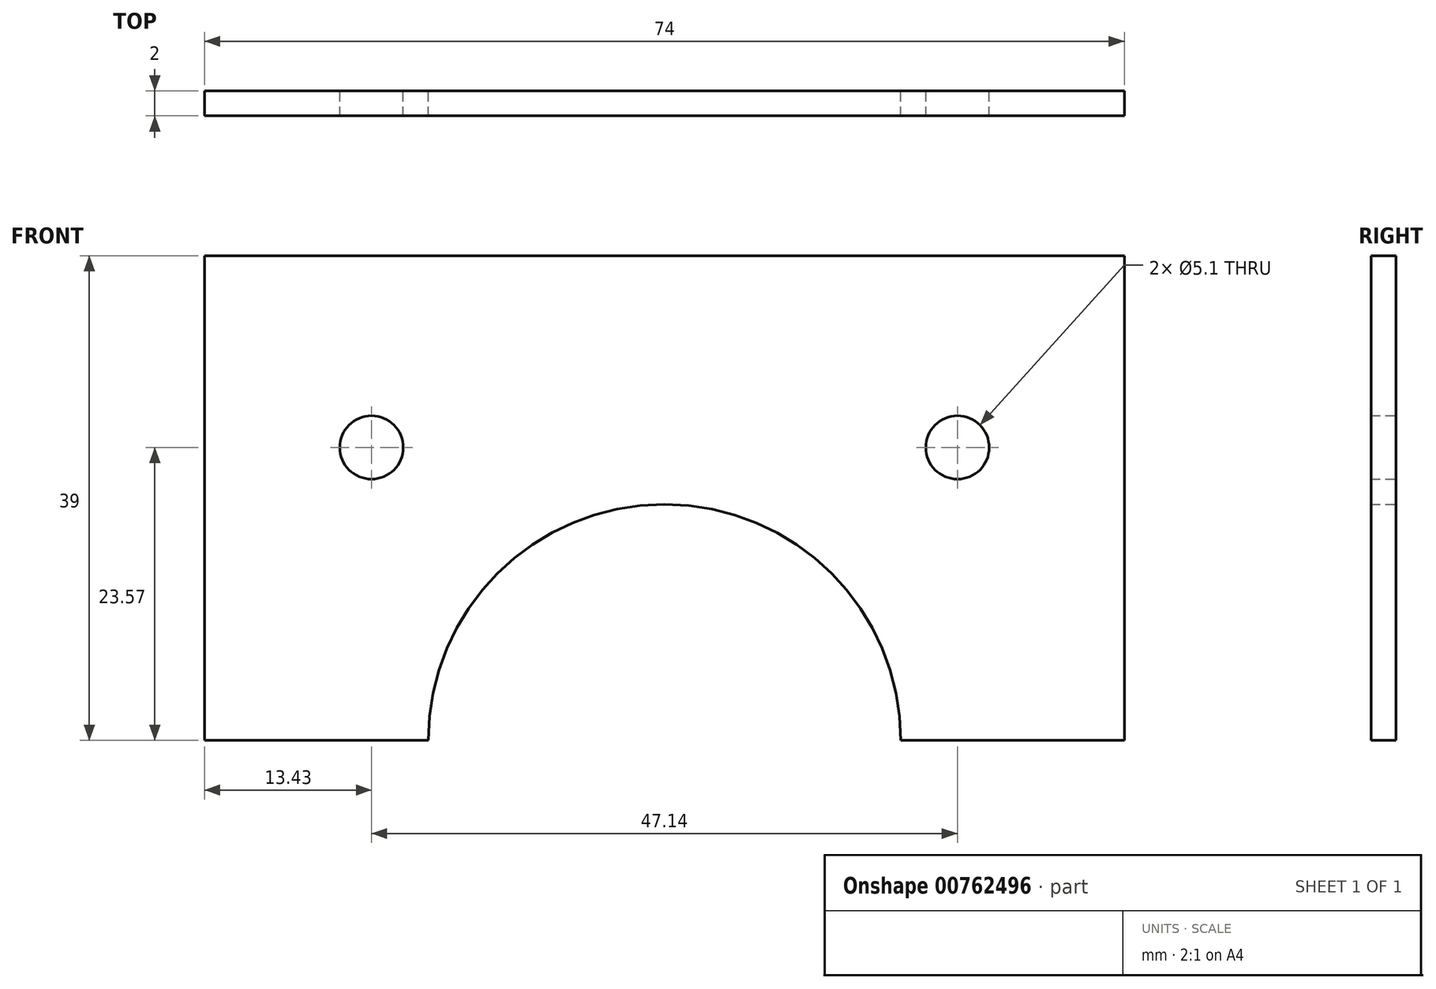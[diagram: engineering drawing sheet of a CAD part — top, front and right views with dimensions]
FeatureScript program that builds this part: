
annotation { "Feature Type Name" : "Feature", "Feature Type Description" : "" }
export const myFeature = defineFeature(function(context is Context, id is Id, definition is map)
    precondition{}
    {
        {
            var Q0;
            Q0=qCreatedBy(makeId("Front.planeOp"),FACE);
            var sketch = newSketch(context, id + "F0", { "sketchPlane" : qUnion([Q0])});
            skLineSegment(sketch, "E0.bottom", {"start": v(0, 0) * mm, "end": v(-18, 0) * mm});
            skLineSegment(sketch, "E0.top", {"start": v(0, 39) * mm, "end": v(-74, 39) * mm});
            skLineSegment(sketch, "E0.left", {"start": v(0, 0) * mm, "end": v(0, 39) * mm});
            skLineSegment(sketch, "E0.right", {"start": v(-74, 0) * mm, "end": v(-74, 39) * mm});
            skLineSegment(sketch, "E1", {"start": v(-37, 19.5) * mm, "end": v(-37, 19) * mm});
            skLineSegment(sketch, "E2", {"start": v(-60.57, 0) * mm, "end": v(-60.57, 39) * mm});
            skLineSegment(sketch, "E3", {"start": v(-13.43, 0) * mm, "end": v(-13.43, 39) * mm});
            skArc(sketch, "E4", {"start": v(-18, 0) * mm, "mid": v(-37, 19) * mm, "end": v(-56, 0) * mm});
            skLineSegment(sketch, "E5.trimOffspring", {"start": v(-56, 0) * mm, "end": v(-74, 0) * mm});
            skLineSegment(sketch, "E6", {"start": v(-60.57, 23.57) * mm, "end": v(-13.43, 23.57) * mm});
            skCircle(sketch, "E7", {"center": v(-60.57, 23.57) * mm, "radius": 2.55 * mm});
            skCircle(sketch, "E8", {"center": v(-13.43, 23.57) * mm, "radius": 2.55 * mm});
            skSolve(sketch);
        }
        {
            var Q0;
            Q0 = qSketchRegion(id + "F0", true);
            extrude(context, id + "F1", {"entities" : qUnion([Q0]), "depth" : 2 * mm, "offsetDistance" : 25 * mm});
        }
    });
